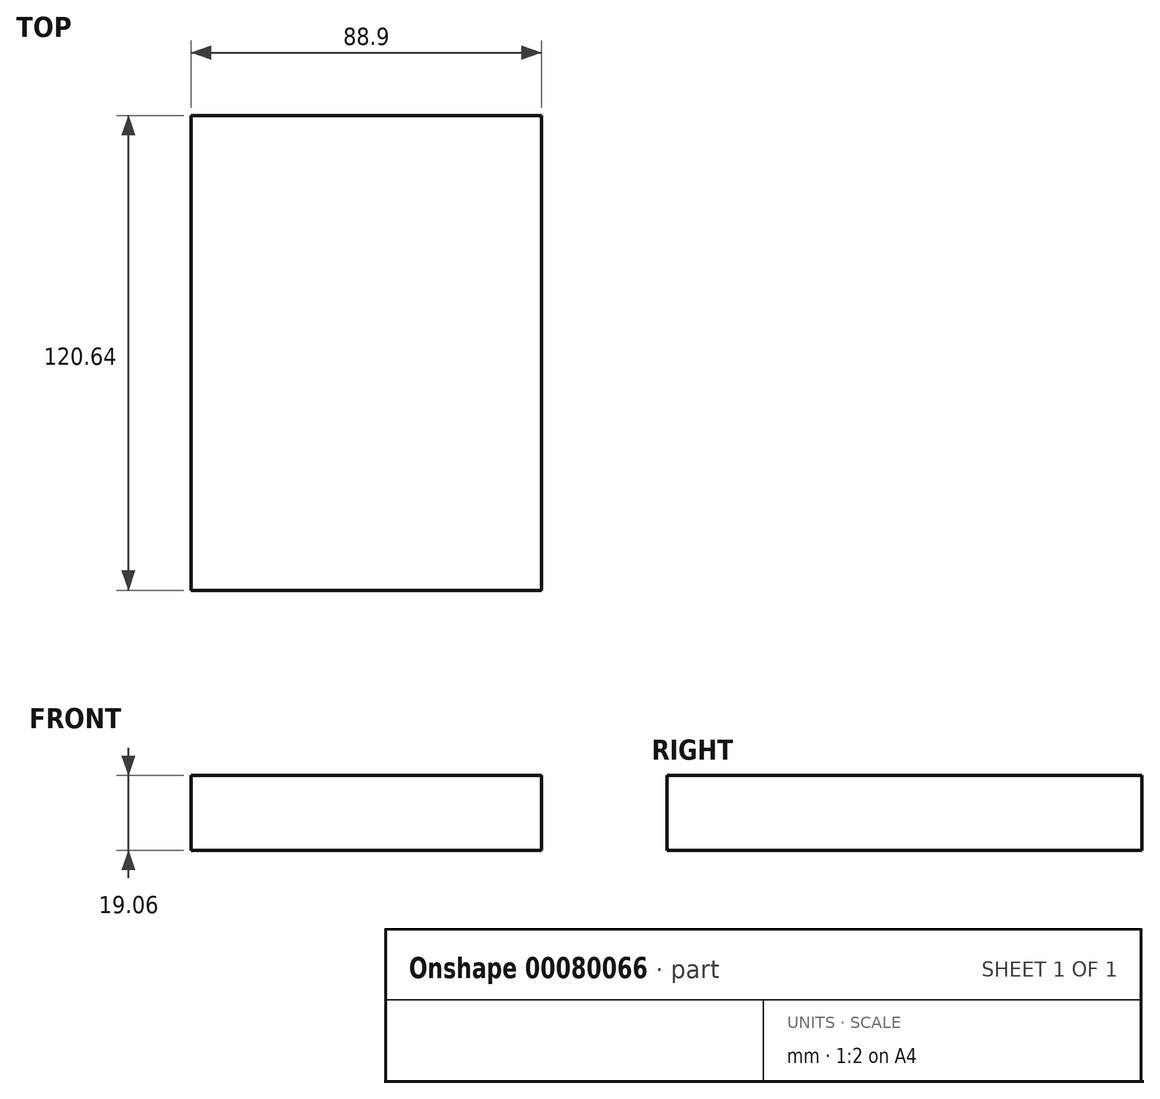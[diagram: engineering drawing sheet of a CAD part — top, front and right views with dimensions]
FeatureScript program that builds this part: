
annotation { "Feature Type Name" : "Feature", "Feature Type Description" : "" }
export const myFeature = defineFeature(function(context is Context, id is Id, definition is map)
    precondition{}
    {
        {
            var Q0;
            Q0=qCreatedBy(makeId("Front.planeOp"),FACE);
            var sketch = newSketch(context, id + "F0", { "sketchPlane" : qUnion([Q0])});
            skLineSegment(sketch, "E0.bottom", {"start": v(-44.45, 9.53) * mm, "end": v(44.45, 9.53) * mm});
            skLineSegment(sketch, "E0.top", {"start": v(-44.45, -9.52) * mm, "end": v(44.45, -9.52) * mm});
            skLineSegment(sketch, "E0.left", {"start": v(-44.45, 9.53) * mm, "end": v(-44.45, -9.52) * mm});
            skLineSegment(sketch, "E0.right", {"start": v(44.45, 9.53) * mm, "end": v(44.45, -9.52) * mm});
            skPoint(sketch, "E0.middle", {"position": v(0, 0) * mm});
            skSolve(sketch);
        }
        {
            var Q0;
            Q0 = qSketchRegion(id + "F0", true);
            extrude(context, id + "F1", {"entities" : qUnion([Q0]), "endBound" : BoundingType.SYMMETRIC, "depth" : 120.65 * mm});
        }
    });
